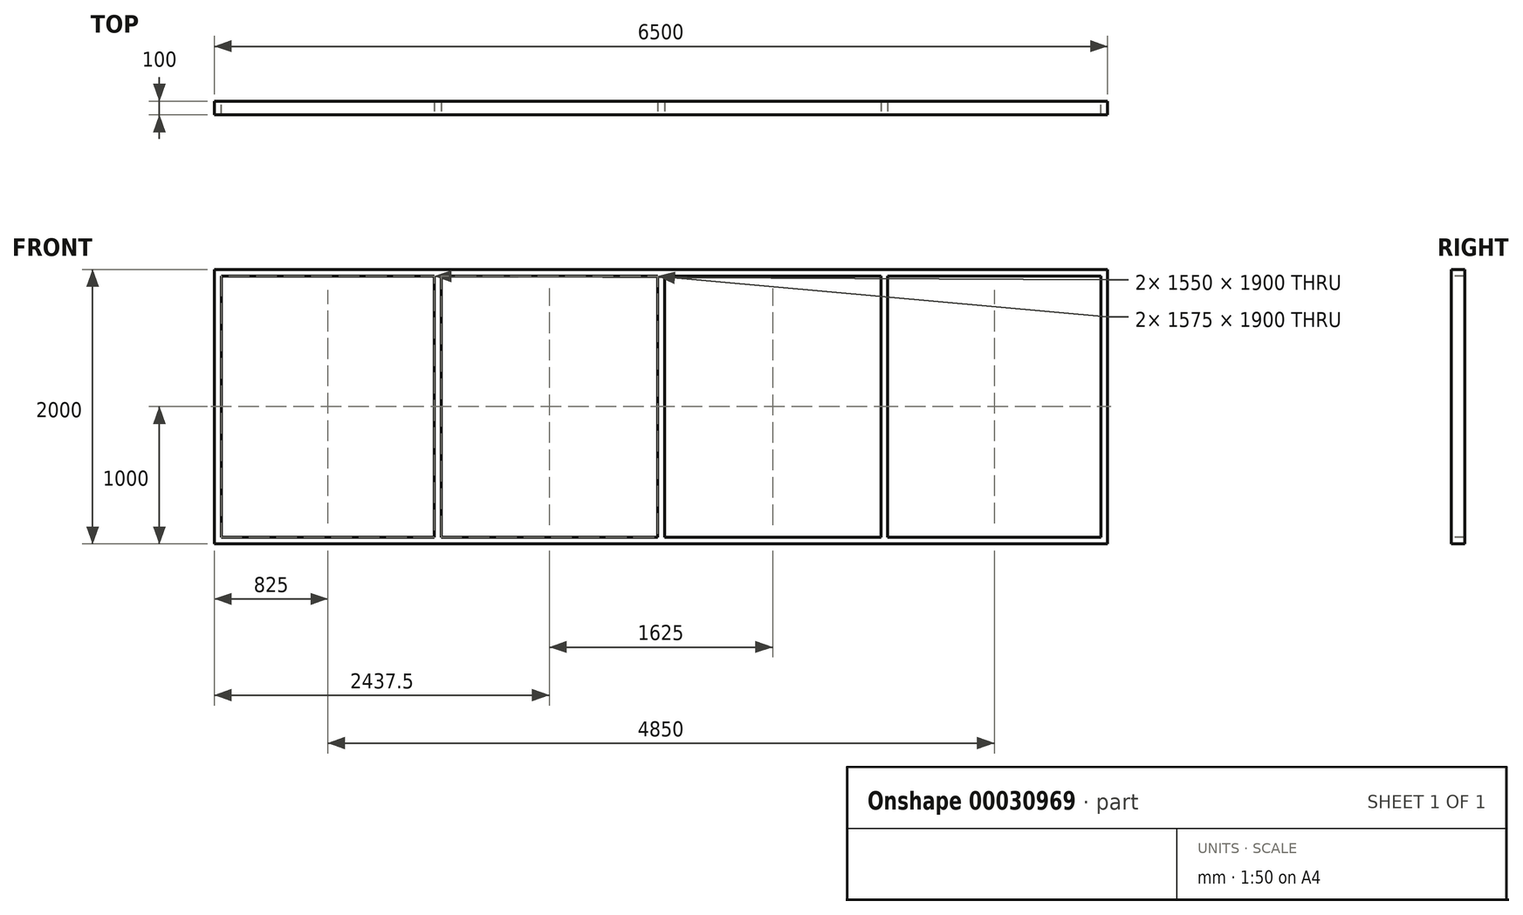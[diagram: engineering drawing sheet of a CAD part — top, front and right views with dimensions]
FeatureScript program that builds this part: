
annotation { "Feature Type Name" : "Feature", "Feature Type Description" : "" }
export const myFeature = defineFeature(function(context is Context, id is Id, definition is map)
    precondition{}
    {
        {
            var Q0;
            Q0=qCreatedBy(makeId("Front.planeOp"),FACE);
            var sketch = newSketch(context, id + "F0", { "sketchPlane" : qUnion([Q0])});
            skLineSegment(sketch, "E0.bottom", {"start": v(0, 0) * mm, "end": v(6500, 0) * mm});
            skLineSegment(sketch, "E0.top", {"start": v(0, 2000) * mm, "end": v(6500, 2000) * mm});
            skLineSegment(sketch, "E0.left", {"start": v(0, 0) * mm, "end": v(0, 2000) * mm});
            skLineSegment(sketch, "E0.right", {"start": v(6500, 0) * mm, "end": v(6500, 2000) * mm});
            skLineSegment(sketch, "E1.0", {"start": v(50, 1950) * mm, "end": v(6450, 1950) * mm});
            skLineSegment(sketch, "E2.0", {"start": v(50, 50) * mm, "end": v(50, 1950) * mm});
            skLineSegment(sketch, "E3.0", {"start": v(50, 50) * mm, "end": v(6450, 50) * mm});
            skLineSegment(sketch, "E4.0", {"start": v(6450, 50) * mm, "end": v(6450, 1950) * mm});
            skSolve(sketch);
        }
        {
            var Q0;
            Q0=makeQuery(id+"F0.imprint","IMPRINT",FACE,{"disambiguationData":[TD([[makeQuery(id+"F0.imprint","IMPRINT",EDGE,{"derivedFrom":sQuery(id+"F0.wireOp",EDGE,"E0.bottom")}),1.0]])]});
            extrude(context, id + "F1", {"entities" : qUnion([Q0]), "depth" : 100 * mm});
        }
        {
            var Q0;
            Q0=makeQuery(id+"F1.opExtrude","CAP_FACE",FACE,{"disambiguationData":[OSD([sQuery(id+"F0.wireOp",EDGE,"E0.bottom"),sQuery(id+"F0.wireOp",EDGE,"E0.top"),sQuery(id+"F0.wireOp",EDGE,"E0.left"),sQuery(id+"F0.wireOp",EDGE,"E0.right"),sQuery(id+"F0.wireOp",EDGE,"E1.0"),sQuery(id+"F0.wireOp",EDGE,"E2.0"),sQuery(id+"F0.wireOp",EDGE,"E3.0"),sQuery(id+"F0.wireOp",EDGE,"E4.0")])],"isStart":false});
            var sketch = newSketch(context, id + "F2", { "sketchPlane" : qUnion([Q0])});
            skLineSegment(sketch, "E5.bottom", {"start": v(1600, 1950) * mm, "end": v(1650, 1950) * mm});
            skLineSegment(sketch, "E5.top", {"start": v(1600, 50) * mm, "end": v(1650, 50) * mm});
            skLineSegment(sketch, "E5.left", {"start": v(1600, 1950) * mm, "end": v(1600, 50) * mm});
            skLineSegment(sketch, "E5.right", {"start": v(1650, 1950) * mm, "end": v(1650, 50) * mm});
            skSolve(sketch);
        }
        {
            var Q0;
            Q0=makeQuery(id+"F2.imprint","IMPRINT",FACE,{"disambiguationData":[TD([[makeQuery(id+"F2.imprint","IMPRINT",EDGE,{"derivedFrom":sQuery(id+"F2.wireOp",EDGE,"E5.bottom")}),-1.0]])]});
            extrude(context, id + "F3", {"entities" : qUnion([Q0]), "operationType" : NewBodyOperationType.ADD, "oppositeDirection" : true, "depth" : 100 * mm});
        }
        {
            var Q0;
            Q0=makeQuery(id+"F3.boolean.opBoolean","MERGE",FACE,{"derivedFrom":[makeQuery(id+"F1.opExtrude","CAP_FACE",FACE,{"disambiguationData":[OSD([sQuery(id+"F0.wireOp",EDGE,"E0.bottom"),sQuery(id+"F0.wireOp",EDGE,"E0.top"),sQuery(id+"F0.wireOp",EDGE,"E0.left"),sQuery(id+"F0.wireOp",EDGE,"E0.right"),sQuery(id+"F0.wireOp",EDGE,"E1.0"),sQuery(id+"F0.wireOp",EDGE,"E2.0"),sQuery(id+"F0.wireOp",EDGE,"E3.0"),sQuery(id+"F0.wireOp",EDGE,"E4.0")])],"isStart":false}),makeQuery(id+"F3.opExtrude","CAP_FACE",FACE,{"disambiguationData":[OSD([sQuery(id+"F2.wireOp",EDGE,"E5.bottom"),sQuery(id+"F2.wireOp",EDGE,"E5.top"),sQuery(id+"F2.wireOp",EDGE,"E5.left"),sQuery(id+"F2.wireOp",EDGE,"E5.right")])],"isStart":true})]});
            var sketch = newSketch(context, id + "F4", { "sketchPlane" : qUnion([Q0])});
            skLineSegment(sketch, "E6.bottom", {"start": v(3225, 1950) * mm, "end": v(3275, 1950) * mm});
            skLineSegment(sketch, "E6.top", {"start": v(3225, 50) * mm, "end": v(3275, 50) * mm});
            skLineSegment(sketch, "E6.left", {"start": v(3225, 1950) * mm, "end": v(3225, 50) * mm});
            skLineSegment(sketch, "E6.right", {"start": v(3275, 1950) * mm, "end": v(3275, 50) * mm});
            skSolve(sketch);
        }
        {
            var Q0;
            Q0=makeQuery(id+"F4.imprint","IMPRINT",FACE,{"disambiguationData":[TD([[makeQuery(id+"F4.imprint","IMPRINT",EDGE,{"derivedFrom":sQuery(id+"F4.wireOp",EDGE,"E6.bottom")}),-1.0]])]});
            extrude(context, id + "F5", {"entities" : qUnion([Q0]), "operationType" : NewBodyOperationType.ADD, "oppositeDirection" : true, "depth" : 100 * mm});
        }
        {
            var Q0;
            Q0=makeQuery(id+"F5.boolean.opBoolean","MERGE",FACE,{"derivedFrom":[makeQuery(id+"F3.boolean.opBoolean","MERGE",FACE,{"derivedFrom":[makeQuery(id+"F1.opExtrude","CAP_FACE",FACE,{"disambiguationData":[OSD([sQuery(id+"F0.wireOp",EDGE,"E0.bottom"),sQuery(id+"F0.wireOp",EDGE,"E0.top"),sQuery(id+"F0.wireOp",EDGE,"E0.left"),sQuery(id+"F0.wireOp",EDGE,"E0.right"),sQuery(id+"F0.wireOp",EDGE,"E1.0"),sQuery(id+"F0.wireOp",EDGE,"E2.0"),sQuery(id+"F0.wireOp",EDGE,"E3.0"),sQuery(id+"F0.wireOp",EDGE,"E4.0")])],"isStart":false}),makeQuery(id+"F3.opExtrude","CAP_FACE",FACE,{"disambiguationData":[OSD([sQuery(id+"F2.wireOp",EDGE,"E5.bottom"),sQuery(id+"F2.wireOp",EDGE,"E5.top"),sQuery(id+"F2.wireOp",EDGE,"E5.left"),sQuery(id+"F2.wireOp",EDGE,"E5.right")])],"isStart":true})]}),makeQuery(id+"F5.opExtrude","CAP_FACE",FACE,{"disambiguationData":[OSD([sQuery(id+"F4.wireOp",EDGE,"E6.bottom"),sQuery(id+"F4.wireOp",EDGE,"E6.top"),sQuery(id+"F4.wireOp",EDGE,"E6.left"),sQuery(id+"F4.wireOp",EDGE,"E6.right")])],"isStart":true})]});
            var sketch = newSketch(context, id + "F6", { "sketchPlane" : qUnion([Q0])});
            skLineSegment(sketch, "E7.bottom", {"start": v(4900, 1950) * mm, "end": v(4850, 1950) * mm});
            skLineSegment(sketch, "E7.top", {"start": v(4900, 50) * mm, "end": v(4850, 50) * mm});
            skLineSegment(sketch, "E7.left", {"start": v(4900, 1950) * mm, "end": v(4900, 50) * mm});
            skLineSegment(sketch, "E7.right", {"start": v(4850, 1950) * mm, "end": v(4850, 50) * mm});
            skSolve(sketch);
        }
        {
            var Q0;
            Q0=makeQuery(id+"F6.imprint","IMPRINT",FACE,{"disambiguationData":[TD([[makeQuery(id+"F6.imprint","IMPRINT",EDGE,{"derivedFrom":sQuery(id+"F6.wireOp",EDGE,"E7.bottom")}),-1.0]])]});
            extrude(context, id + "F7", {"entities" : qUnion([Q0]), "operationType" : NewBodyOperationType.ADD, "oppositeDirection" : true, "depth" : 100 * mm});
        }
    });
